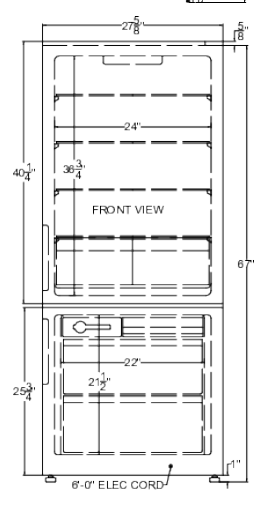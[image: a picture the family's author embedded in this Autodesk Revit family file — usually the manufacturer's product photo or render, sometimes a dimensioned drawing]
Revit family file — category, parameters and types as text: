
# Revit family: QF_Summit_FFBF279SSX_Freezer_Refrigerator
name_source: partatom
category: Specialty Equipment
units: mm (PartAtom-declared; Revit-internal decimal feet)

## family parameters
Always vertical = Yes
Cut with Voids When Loaded = No
Part Type = Normal
Room Calculation Point = No
Round Connector Dimension = Use Diameter
Shared = No
Work Plane-Based = No

## types (1)
- QF_Summit_FFBF279SSX_Freezer_Refrigerator
    Apparent Power = 0 VA
    BTUH = 0.0 Btu/h
    Conn Conduit = Yes
    Cycle = 60 Hz
    Default Elevation = 0"
    Depth = 26 3/4"
    Description = Freezer Refrigerator
    Elec Conn Connection Height = 0"
    Elec Conn RI Height = 0"
    FL Amps = 2 A
    Foodservice Equipment Identifier = Yes
    Height = 67"
    Identify Quantity as Lot = Yes
    Length = 27 5/8"
    Manufacturer = Summit
    Max Overcurrent Protection = 0 A
    Min Ckt Ampacity = 0 A
    Model = FFBF279SSX
    Number of Poles = 1
    Phase = 1
    Refrigerant Type = R600a
    Refrigerant Volume = 0.00 kip
    Volts = 115 V
    Watts = 230 W
    Weight in Pounds = 177

## geometry (parser evidence)
native form markers: Sweep x5
no freeform markers — native parametric forms only
